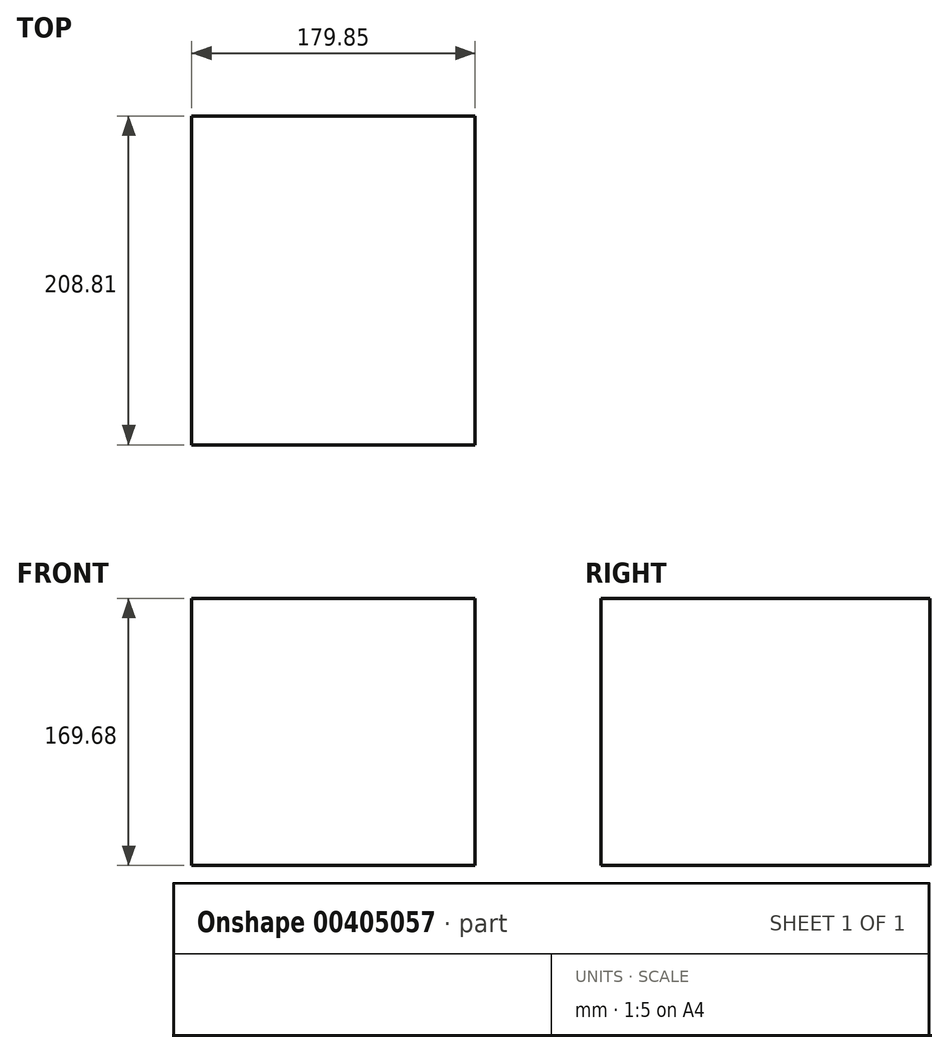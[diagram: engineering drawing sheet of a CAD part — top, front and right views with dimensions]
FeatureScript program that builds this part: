
annotation { "Feature Type Name" : "Feature", "Feature Type Description" : "" }
export const myFeature = defineFeature(function(context is Context, id is Id, definition is map)
    precondition{}
    {
        {
            var Q0;
            Q0=qCreatedBy(makeId("Right.planeOp"),FACE);
            var sketch = newSketch(context, id + "F0", { "sketchPlane" : qUnion([Q0])});
            skLineSegment(sketch, "E0.bottom", {"start": v(0, 0) * mm, "end": v(-208.8, 0) * mm});
            skLineSegment(sketch, "E0.top", {"start": v(0, 169.68) * mm, "end": v(-208.8, 169.68) * mm});
            skLineSegment(sketch, "E0.left", {"start": v(0, 0) * mm, "end": v(0, 169.68) * mm});
            skLineSegment(sketch, "E0.right", {"start": v(-208.8, 0) * mm, "end": v(-208.8, 169.68) * mm});
            skSolve(sketch);
        }
        {
            var Q0;
            Q0=makeQuery(id+"F0.imprint","IMPRINT",FACE,{"disambiguationData":[TD([[makeQuery(id+"F0.imprint","IMPRINT",EDGE,{"derivedFrom":sQuery(id+"F0.wireOp",EDGE,"E0.bottom")}),-1.0]])]});
            extrude(context, id + "F1", {"entities" : qUnion([Q0]), "depth" : 179.85 * mm});
        }
    });
